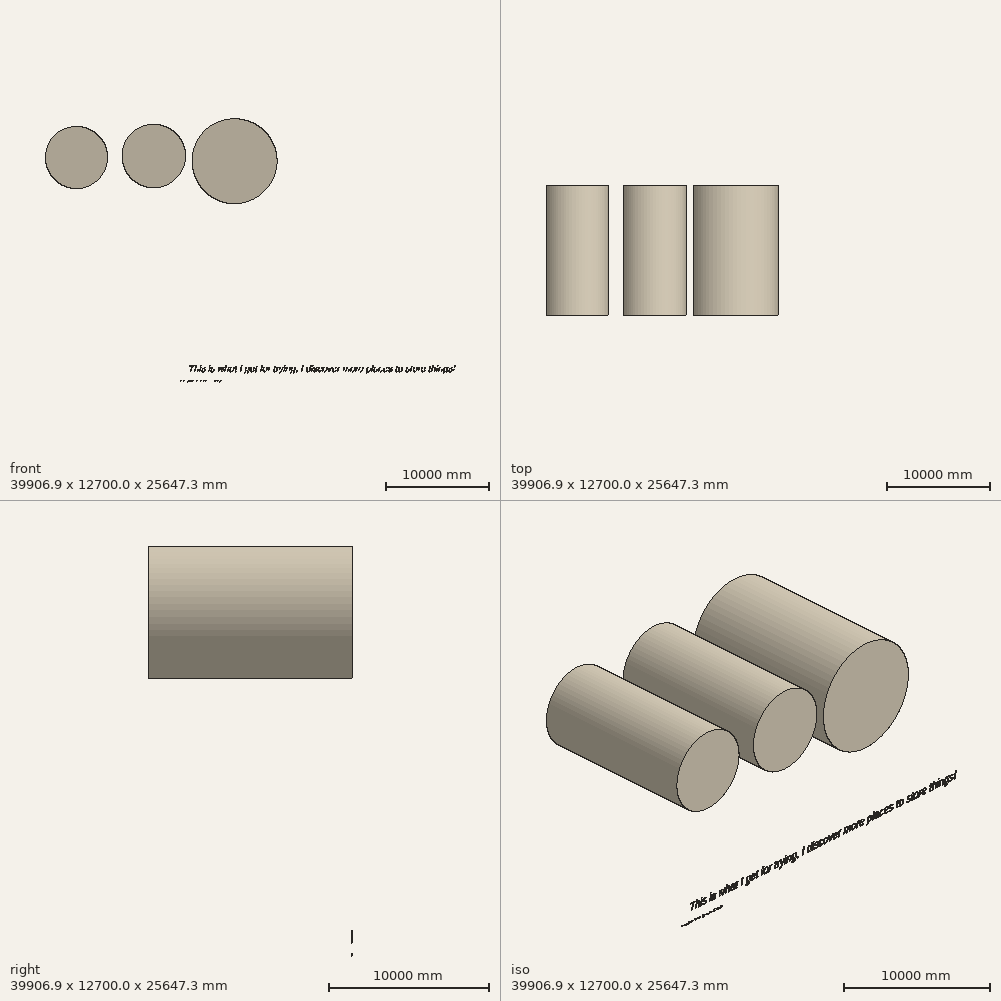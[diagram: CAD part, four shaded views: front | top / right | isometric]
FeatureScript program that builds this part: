
annotation { "Feature Type Name" : "Feature", "Feature Type Description" : "" }
export const myFeature = defineFeature(function(context is Context, id is Id, definition is map)
    precondition{}
    {
        {
            var Q0;
            Q0=qCreatedBy(makeId("Front.planeOp"),FACE);
            var sketch = newSketch(context, id + "F0", { "sketchPlane" : qUnion([Q0])});
            skText(sketch, "E0", { "text": "(90+4)-(80+3)=(90-80)+(4-3)=(10+1)=(11)", "fontName": "OpenSans-Regular.ttf"});
            const initialGuessF0  = {"E0": [0.20042, -0.1974, 1, 0, 0.16812]};
            skSetInitialGuess(sketch, initialGuessF0);
            skSolve(sketch);
        }
        {
            var Q0;
            Q0 = qSketchRegion(id + "F0", true);
            extrude(context, id + "F1", {"entities" : qUnion([Q0]), "depth" : 25.4 * mm, "offsetDistance" : 25.4 * mm});
        }
        {
            var Q0;
            Q0=qCreatedBy(makeId("Front.planeOp"),FACE);
            var sketch = newSketch(context, id + "F2", { "sketchPlane" : qUnion([Q0])});
            skText(sketch, "E1", { "text": "This is what I get for trying, I discover more places to store things!", "fontName": "Arimo-Italic.ttf"});
            const initialGuessF2  = {"E1": [1.0433, 0.76334, 1, 0, 0.64357]};
            skSetInitialGuess(sketch, initialGuessF2);
            skSolve(sketch);
        }
        {
            var Q0;
            Q0 = qSketchRegion(id + "F2", true);
            extrude(context, id + "F3", {"entities" : qUnion([Q0]), "depth" : 25.4 * mm, "offsetDistance" : 25.4 * mm});
        }
        {
            var Q0;
            Q0=qCreatedBy(makeId("Front.planeOp"),FACE);
            var sketch = newSketch(context, id + "F4", { "sketchPlane" : qUnion([Q0])});
            skCircle(sketch, "E2", {"center": v(-9864.44, 21631.06) * mm, "radius": 3027.75 * mm});
            skCircle(sketch, "E3", {"center": v(-2343.63, 21773.06) * mm, "radius": 3092.19 * mm});
            skCircle(sketch, "E4", {"center": v(5518, 21276.03) * mm, "radius": 4136.87 * mm});
            skSolve(sketch);
        }
        {
            var Q0;
            Q0 = qSketchRegion(id + "F4", true);
            extrude(context, id + "F5", {"entities" : qUnion([Q0]), "depth" : 12700 * mm, "offsetDistance" : 25.4 * mm});
        }
    });
